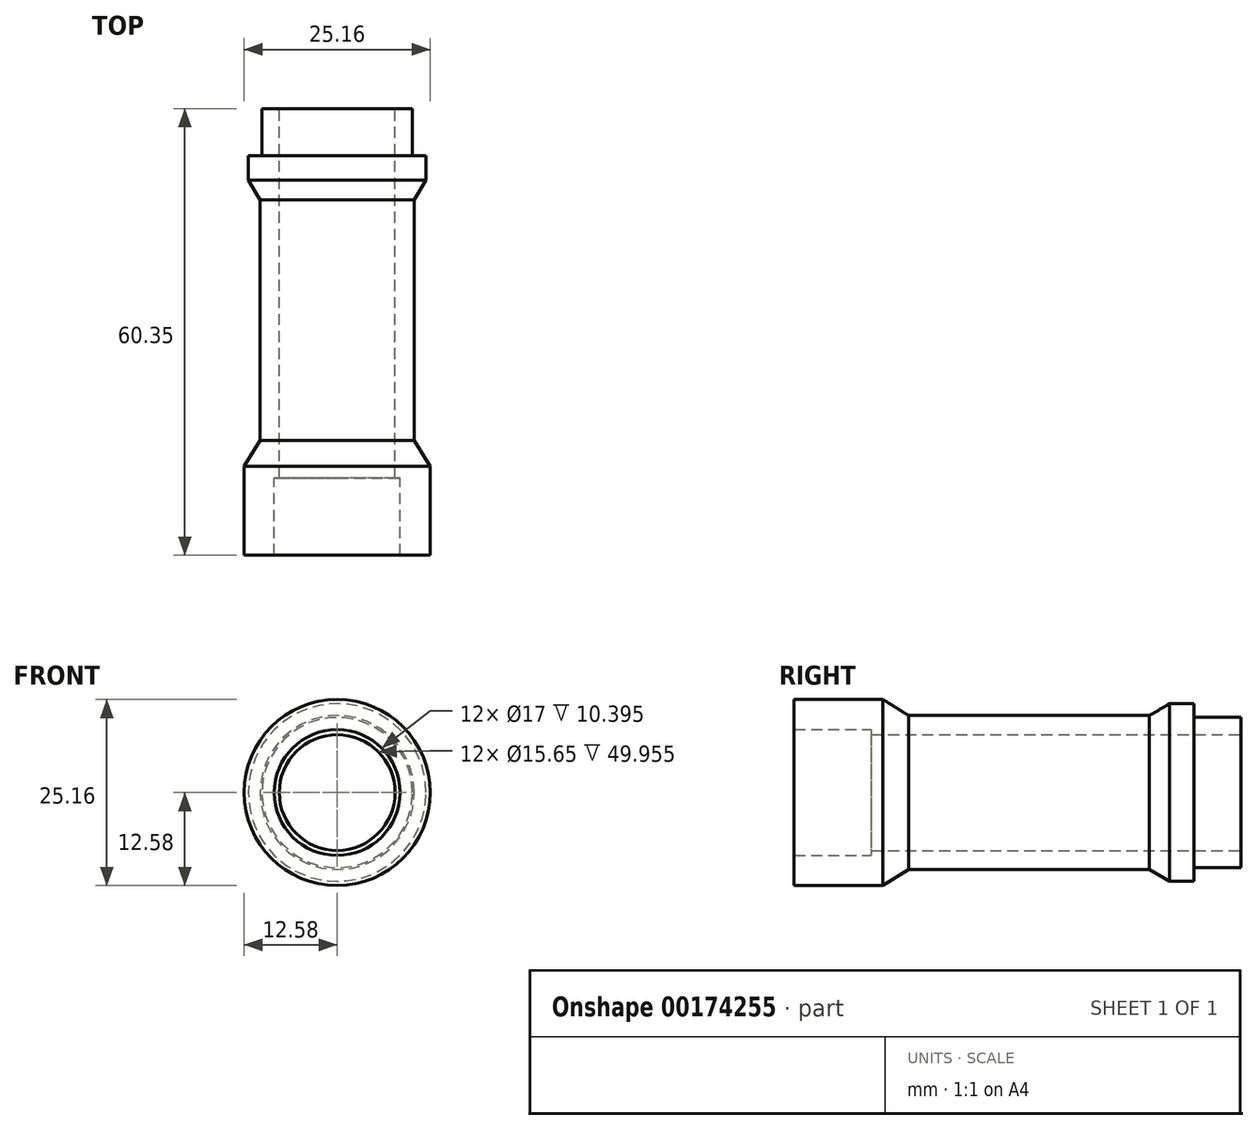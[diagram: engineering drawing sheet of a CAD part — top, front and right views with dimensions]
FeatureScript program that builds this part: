
annotation { "Feature Type Name" : "Feature", "Feature Type Description" : "" }
export const myFeature = defineFeature(function(context is Context, id is Id, definition is map)
    precondition{}
    {
        {
            var Q0;
            Q0=qCreatedBy(makeId("Top.planeOp"),FACE);
            var sketch = newSketch(context, id + "F0", { "sketchPlane" : qUnion([Q0])});
            skLineSegment(sketch, "E0", {"start": v(12.58, 12) * mm, "end": v(10.4, 15.5) * mm});
            skLineSegment(sketch, "E1", {"start": v(10.4, 15.5) * mm, "end": v(10.4, 48) * mm});
            skLineSegment(sketch, "E2", {"start": v(10.4, 48) * mm, "end": v(12, 50.7) * mm});
            skLineSegment(sketch, "E3", {"start": v(12, 50.7) * mm, "end": v(12, 54) * mm});
            skLineSegment(sketch, "E4", {"start": v(12, 54) * mm, "end": v(10.15, 54) * mm});
            skLineSegment(sketch, "E5", {"start": v(10.15, 54) * mm, "end": v(10.15, 60.35) * mm});
            skLineSegment(sketch, "E6", {"start": v(10.15, 60.35) * mm, "end": v(0, 60.35) * mm});
            skLineSegment(sketch, "E7", {"start": v(0, 60.35) * mm, "end": v(0, 0) * mm});
            skLineSegment(sketch, "E8.MirrorCS", {"start": v(-10.15, 60.35) * mm, "end": v(0, 60.35) * mm, "construction": true});
            skLineSegment(sketch, "E9.MirrorCS", {"start": v(-10.15, 54) * mm, "end": v(-10.15, 60.35) * mm, "construction": true});
            skLineSegment(sketch, "E10.MirrorCS", {"start": v(-12, 54) * mm, "end": v(-10.15, 54) * mm, "construction": true});
            skLineSegment(sketch, "E11.MirrorCS", {"start": v(-12, 50.7) * mm, "end": v(-12, 54) * mm, "construction": true});
            skLineSegment(sketch, "E12.MirrorCS", {"start": v(-10.4, 48) * mm, "end": v(-12, 50.7) * mm, "construction": true});
            skLineSegment(sketch, "E13.MirrorCS", {"start": v(-10.4, 15.5) * mm, "end": v(-10.4, 48) * mm, "construction": true});
            skLineSegment(sketch, "E14.MirrorCS", {"start": v(-12.57, 12) * mm, "end": v(-10.4, 15.5) * mm, "construction": true});
            skLineSegment(sketch, "E15", {"start": v(12.58, 12) * mm, "end": v(12.57, 0) * mm});
            skLineSegment(sketch, "E16.MirrorCS", {"start": v(-12.57, 12) * mm, "end": v(-12.57, 0) * mm, "construction": true});
            skLineSegment(sketch, "E17", {"start": v(0, 0) * mm, "end": v(12.57, 0) * mm});
            skLineSegment(sketch, "E18", {"start": v(0, 0) * mm, "end": v(-12.57, 0) * mm, "construction": true});
            skLineSegment(sketch, "E19", {"start": v(8.5, 0) * mm, "end": v(8.5, 10.4) * mm});
            skLineSegment(sketch, "E20.MirrorCS", {"start": v(-8.5, 0) * mm, "end": v(-8.5, 10.4) * mm, "construction": true});
            skLineSegment(sketch, "E21", {"start": v(8.5, 10.4) * mm, "end": v(7.83, 10.4) * mm});
            skLineSegment(sketch, "E22", {"start": v(7.82, 10.4) * mm, "end": v(7.82, 60.35) * mm});
            skLineSegment(sketch, "E23.MirrorCS", {"start": v(-7.83, 10.4) * mm, "end": v(-7.83, 60.35) * mm, "construction": true});
            skLineSegment(sketch, "E24", {"start": v(-8.5, 10.4) * mm, "end": v(-7.83, 10.4) * mm, "construction": true});
            skSolve(sketch);
        }
        {
            var Q0;
            Q0=makeQuery(id+"F0.imprint","IMPRINT",FACE,{"disambiguationData":[TD([[makeQuery(id+"F0.imprint","IMPRINT",EDGE,{"derivedFrom":sQuery(id+"F0.wireOp",EDGE,"E0")}),1.0]])]});
            var Q1;
            Q1=sQuery(id+"F0.wireOp",EDGE,"E7");
            revolve(context, id + "F1", {"entities" : qUnion([Q0]), "axis" : qUnion([Q1]), "revolveType" : RevolveType.FULL});
        }
    });
